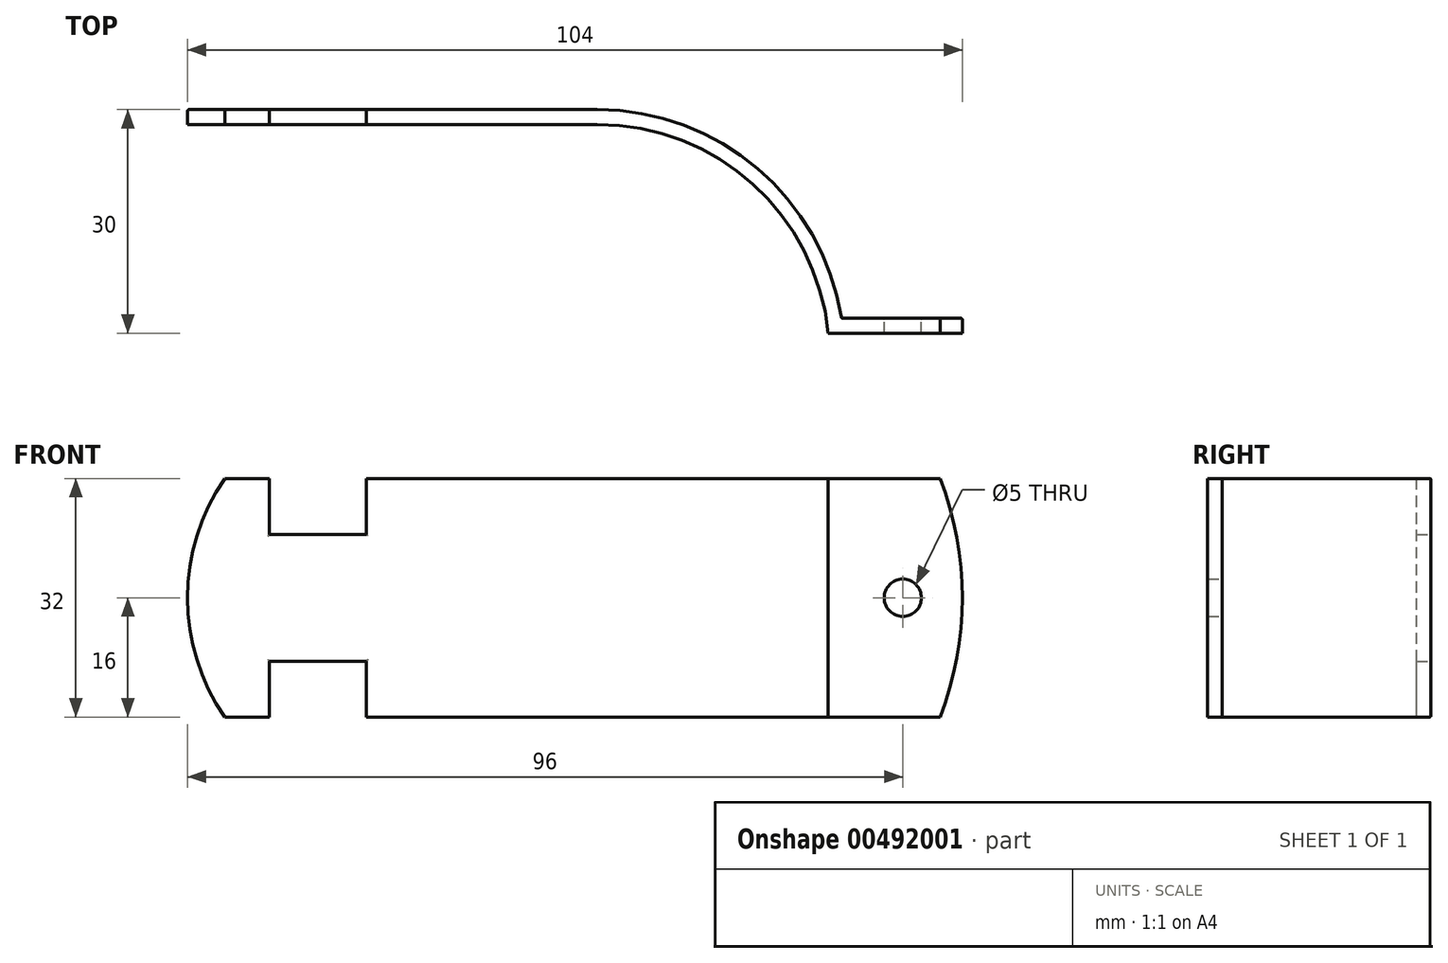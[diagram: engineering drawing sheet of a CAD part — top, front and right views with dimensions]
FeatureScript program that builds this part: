
annotation { "Feature Type Name" : "Feature", "Feature Type Description" : "" }
export const myFeature = defineFeature(function(context is Context, id is Id, definition is map)
    precondition{}
    {
        {
            var Q0;
            Q0=qCreatedBy(makeId("Top.planeOp"),FACE);
            var sketch = newSketch(context, id + "F0", { "sketchPlane" : qUnion([Q0])});
            skLineSegment(sketch, "E0.bottom", {"start": v(27.5, -1) * mm, "end": v(-27.5, -1) * mm});
            skLineSegment(sketch, "E0.top", {"start": v(27.5, 1) * mm, "end": v(-27.5, 1) * mm});
            skLineSegment(sketch, "E0.right", {"start": v(-27.5, -1) * mm, "end": v(-27.5, 1) * mm});
            skPoint(sketch, "E0.middle", {"position": v(0, 0) * mm});
            skLineSegment(sketch, "E1", {"start": v(-27.5, -8.41) * mm, "end": v(58.5, -8.41) * mm, "construction": true});
            skLineSegment(sketch, "E2", {"start": v(27.5, -1) * mm, "end": v(27.5, -29) * mm, "construction": true});
            skLineSegment(sketch, "E3", {"start": v(27.5, -29) * mm, "end": v(58.5, -29) * mm, "construction": true});
            skArc(sketch, "E4", {"start": v(58.5, -29) * mm, "mid": v(48.39, -9.04) * mm, "end": v(27.5, -1) * mm});
            skLineSegment(sketch, "E5", {"start": v(58.5, -29) * mm, "end": v(76.5, -29) * mm});
            skArc(sketch, "E6.0", {"start": v(60.26, -27) * mm, "mid": v(49.05, -6.95) * mm, "end": v(27.5, 1) * mm});
            skLineSegment(sketch, "E7.0", {"start": v(60.26, -27) * mm, "end": v(76.5, -27) * mm});
            skLineSegment(sketch, "E8", {"start": v(76.5, -27) * mm, "end": v(76.5, -29) * mm});
            skSolve(sketch);
        }
        {
            var Q0;
            Q0=qSketchRegion(id+"F0",true);
            extrude(context, id + "F1", {"entities" : qUnion([Q0]), "endBound" : BoundingType.SYMMETRIC, "depth" : 32 * mm});
        }
        {
            var Q0;
            Q0=makeQuery(id+"F1.opExtrude","SWEPT_FACE",FACE,{"disambiguationData":[OSD([sQuery(id+"F0.wireOp",EDGE,"E5")])]});
            var sketch = newSketch(context, id + "F2", { "sketchPlane" : qUnion([Q0])});
            skLineSegment(sketch, "E9", {"start": v(76.5, 16) * mm, "end": v(73.5, 16) * mm});
            skLineSegment(sketch, "E10", {"start": v(76.5, -16) * mm, "end": v(73.5, -16) * mm});
            skArc(sketch, "E11", {"start": v(73.5, -16) * mm, "mid": v(76.5, 0) * mm, "end": v(73.5, 16) * mm});
            skSolve(sketch);
        }
        {
            var Q0;
            {var subQ0=sQuery(id+"F2.wireOp",EDGE,"E9");Q0=makeQuery(id+"F2.imprint","IMPRINT",FACE,{"disambiguationData":[TD([[makeQuery(id+"F2.imprint","IMPRINT",EDGE,{"derivedFrom":subQ0}),-1.0]])]});}
            var Q1;
            {var subQ0=sQuery(id+"F2.wireOp",EDGE,"E10");Q1=makeQuery(id+"F2.imprint","IMPRINT",FACE,{"disambiguationData":[TD([[makeQuery(id+"F2.imprint","IMPRINT",EDGE,{"derivedFrom":subQ0}),1.0]])]});}
            extrude(context, id + "F3", {"entities" : qUnion([Q0, Q1]), "operationType" : NewBodyOperationType.REMOVE, "endBound" : BoundingType.SYMMETRIC, "oppositeDirection" : true, "depth" : 25 * mm});
        }
        {
            var Q0;
            Q0=makeQuery(id+"F1.opExtrude","SWEPT_FACE",FACE,{"disambiguationData":[OSD([sQuery(id+"F0.wireOp",EDGE,"E0.top")])]});
            var sketch = newSketch(context, id + "F4", { "sketchPlane" : qUnion([Q0])});
            skLineSegment(sketch, "E12.0", {"start": v(27.5, 16) * mm, "end": v(27.5, -16) * mm});
            skLineSegment(sketch, "E13", {"start": v(27.5, -16) * mm, "end": v(22.5, -16) * mm});
            skLineSegment(sketch, "E14", {"start": v(27.5, 16) * mm, "end": v(22.5, 16) * mm});
            skArc(sketch, "E15", {"start": v(22.5, -16) * mm, "mid": v(27.5, 0) * mm, "end": v(22.5, 16) * mm});
            skSolve(sketch);
        }
        {
            var Q0;
            Q0=qSketchRegion(id+"F4",true);
            extrude(context, id + "F5", {"entities" : qUnion([Q0]), "operationType" : NewBodyOperationType.REMOVE, "endBound" : BoundingType.SYMMETRIC, "depth" : 25 * mm});
        }
        {
            var Q0;
            Q0=makeQuery(id+"F1.opExtrude","SWEPT_FACE",FACE,{"disambiguationData":[OSD([sQuery(id+"F0.wireOp",EDGE,"E0.top")])]});
            var sketch = newSketch(context, id + "F6", { "sketchPlane" : qUnion([Q0])});
            skLineSegment(sketch, "E16", {"start": v(27.5, 0) * mm, "end": v(10, 0) * mm, "construction": true});
            skPoint(sketch, "E16.endSnap0", {"position": v(27.5, 0) * mm});
            skLineSegment(sketch, "E17.bottom", {"start": v(3.5, -8.5) * mm, "end": v(16.5, -8.5) * mm});
            skLineSegment(sketch, "E17.top", {"start": v(3.5, 8.5) * mm, "end": v(16.5, 8.5) * mm});
            skPoint(sketch, "E17.middle", {"position": v(10, 0) * mm});
            skLineSegment(sketch, "E18", {"start": v(16.5, -16) * mm, "end": v(16.5, -8.5) * mm});
            skLineSegment(sketch, "E19", {"start": v(3.5, -16) * mm, "end": v(3.5, -8.5) * mm});
            skLineSegment(sketch, "E20.0", {"start": v(3.5, -16) * mm, "end": v(16.5, -16) * mm});
            skPoint(sketch, "E21.orphan", {"position": v(22.5, -16) * mm});
            skPoint(sketch, "E22.orphan", {"position": v(16.5, -13.95) * mm});
            skPoint(sketch, "E23.orphan", {"position": v(3.5, -14.88) * mm});
            skPoint(sketch, "E24.orphan", {"position": v(-27.5, -16) * mm});
            skLineSegment(sketch, "E25.trimOffspring", {"start": v(3.5, 8.5) * mm, "end": v(3.5, 16) * mm});
            skLineSegment(sketch, "E26.trimOffspring", {"start": v(16.5, 8.5) * mm, "end": v(16.5, 16) * mm});
            skLineSegment(sketch, "E27.0", {"start": v(3.5, 16) * mm, "end": v(16.5, 16) * mm});
            skPoint(sketch, "E28.orphan", {"position": v(22.5, 16) * mm});
            skPoint(sketch, "E29.orphan", {"position": v(-27.5, 16) * mm});
            skSolve(sketch);
        }
        {
            var Q0;
            Q0=qSketchRegion(id+"F6",true);
            extrude(context, id + "F7", {"entities" : qUnion([Q0]), "operationType" : NewBodyOperationType.REMOVE, "endBound" : BoundingType.SYMMETRIC, "oppositeDirection" : true, "depth" : 25 * mm});
        }
        {
            var Q0;
            Q0=makeQuery(id+"F1.opExtrude","SWEPT_FACE",FACE,{"disambiguationData":[OSD([sQuery(id+"F0.wireOp",EDGE,"E7.0")])]});
            var sketch = newSketch(context, id + "F8", { "sketchPlane" : qUnion([Q0])});
            skLineSegment(sketch, "E30", {"start": v(-68.5, 16) * mm, "end": v(-68.5, -16) * mm, "construction": true});
            skLineSegment(sketch, "E31.0", {"start": v(-60.26, 16) * mm, "end": v(-73.5, 16) * mm, "construction": true});
            skLineSegment(sketch, "E32.0", {"start": v(-60.26, -16) * mm, "end": v(-73.5, -16) * mm, "construction": true});
            skCircle(sketch, "E33", {"center": v(-68.5, 0) * mm, "radius": 2.5 * mm});
            skSolve(sketch);
        }
        {
            var Q0;
            Q0=qSketchRegion(id+"F8",true);
            extrude(context, id + "F9", {"entities" : qUnion([Q0]), "operationType" : NewBodyOperationType.REMOVE, "endBound" : BoundingType.SYMMETRIC, "oppositeDirection" : true, "depth" : 25 * mm});
        }
        {
            var Q0;
            Q0=makeQuery(id+"F1.opExtrude","SWEPT_FACE",FACE,{"disambiguationData":[OSD([sQuery(id+"F0.wireOp",EDGE,"E7.0")])]});
            var Q1;
            Q1=makeQuery(id+"F1.opExtrude","SWEPT_FACE",FACE,{"disambiguationData":[OSD([sQuery(id+"F0.wireOp",EDGE,"E6.0")])]});
            var Q2;
            Q2=makeQuery(id+"F1.opExtrude","SWEPT_FACE",FACE,{"disambiguationData":[OSD([sQuery(id+"F0.wireOp",EDGE,"E0.top")])]});
            fillet(context, id + "F10", {"entities" : qUnion([Q0, Q1, Q2]), "radius" : .2 * mm, "tangentPropagation" : true, "allowEdgeOverflow" : false});
        }
    });
